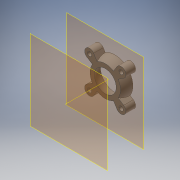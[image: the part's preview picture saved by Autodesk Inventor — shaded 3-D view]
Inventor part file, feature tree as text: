
AUTODESK INVENTOR PART (.ipt)
format: ipt  version: 2017 (Build 210142000, 142)  size: 373,760 bytes
history: native  units: in
note: dims shown in document units (in); Inventor stores cm internally (conversion verified against a paired STEP export)
features: sketch x7, other x4, extrude x2, plane x2, projected_geometry x1
ambient origin geometry x8: Origin, YZ Plane, XZ Plane, XY Plane, X Axis, Y Axis, Z Axis, Center Point
bodies: Solid1 (feature_tree)
feature tree (16):
  other  "shifter cover.ipt"
  extrude  "Extrusion1"  Depth=0.3937in TaperAngle=0.0deg
  extrude  "Extrusion2"  Depth=0.3937in TaperAngle=0.0deg
  other  "Solid1::shifter cover.ipt"
  other  "TaggingFeature1"
  sketch  "Sketch1"  dims[d0=0.3937in d1=0.3937in d2=0.0in]
  sketch  "Sketch2"  dims[d3=0.1378in d4=0.3937in d5=0.0in]
  sketch  "Sketch3"
  sketch  "Sketch4"
  sketch  "Sketch5"
  plane  "Work Plane1"
  plane  "Work Plane2"
  other  "Work Axis1"
  sketch  "Sketch6"
  projected_geometry  "Projected Loop1"
  sketch  "Sketch7"
